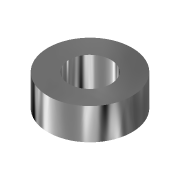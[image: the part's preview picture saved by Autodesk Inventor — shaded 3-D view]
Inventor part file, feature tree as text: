
AUTODESK INVENTOR PART (.ipt)
format: ipt  version: 2022 (Build 260153000, 153)  size: 95,232 bytes
history: native  units: in
note: dims shown in document units (in); Inventor stores cm internally (conversion verified against a paired STEP export)
features: extrude x1, sketch x1
ambient origin geometry x8: Origin, YZ Plane, XZ Plane, XY Plane, X Axis, Y Axis, Z Axis, Center Point
bodies: Solid1 (feature_tree)
feature tree (2):
  extrude  "Extrusion1"  Depth=0.1866in
  sketch  "Sketch1"  dims[d0=0.4988in d1=0.2492in d2=0.1866in d3=0.0in]
